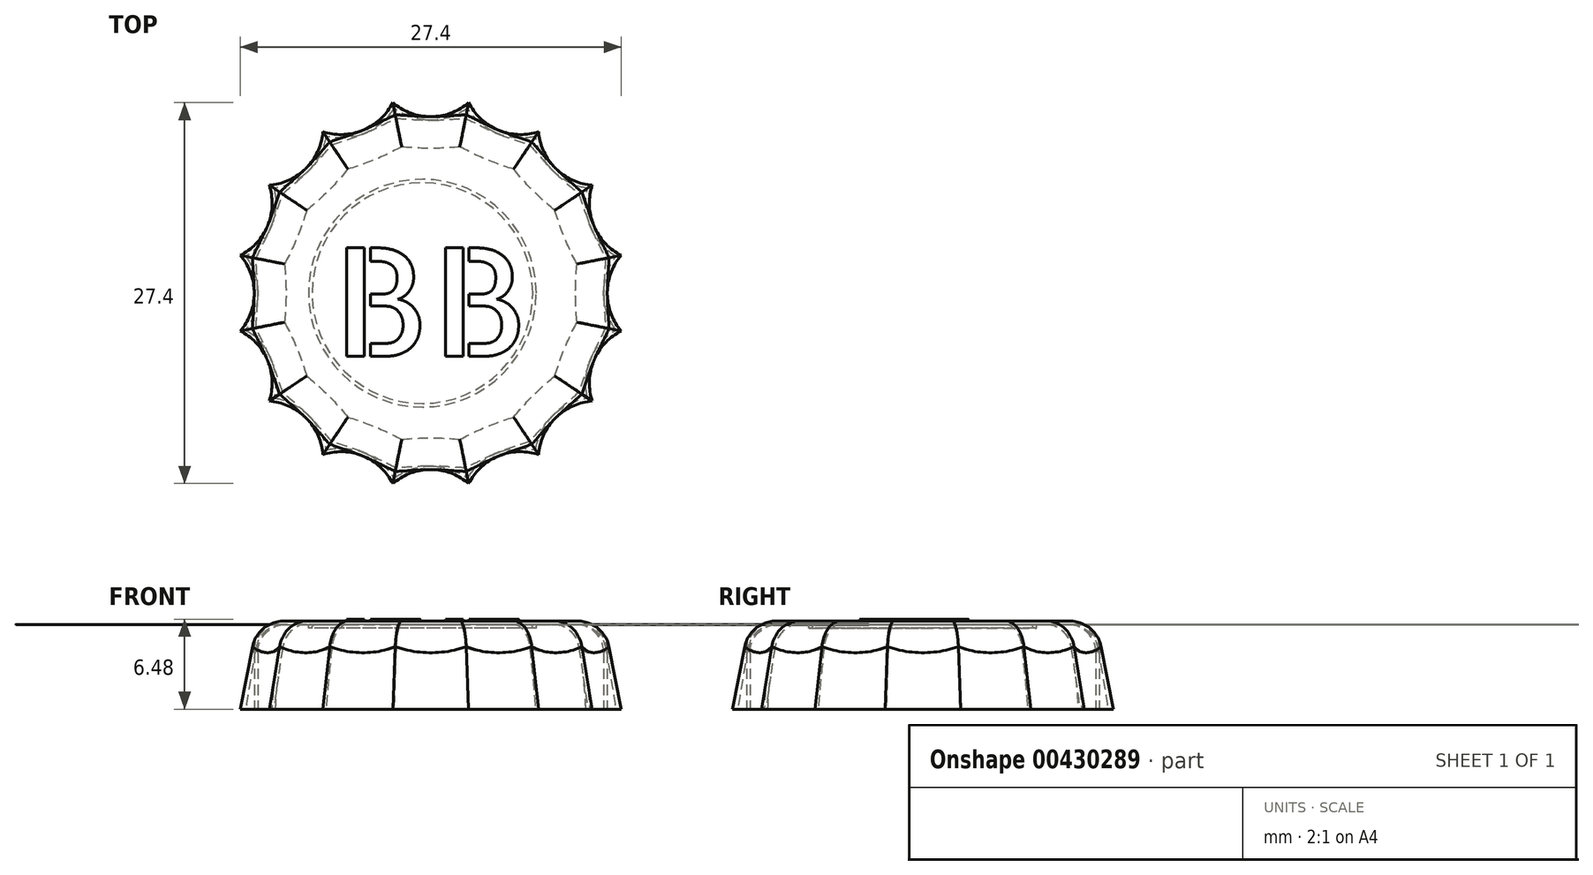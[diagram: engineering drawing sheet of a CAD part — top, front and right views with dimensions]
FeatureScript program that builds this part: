
annotation { "Feature Type Name" : "Feature", "Feature Type Description" : "" }
export const myFeature = defineFeature(function(context is Context, id is Id, definition is map)
    precondition{}
    {
        {
            var Q0;
            Q0=qCreatedBy(makeId("Top.planeOp"),FACE);
            var sketch = newSketch(context, id + "F0", { "sketchPlane" : qUnion([Q0])});
            skCircle(sketch, "E0", {"center": v(0, 0) * mm, "radius": 12.7 * mm, "construction": true});
            skCircle(sketch, "E1.0", {"center": v(0, 0) * mm, "radius": 13.97 * mm});
            skArc(sketch, "E2", {"start": v(-2.73, 13.7) * mm, "mid": v(0, 12.7) * mm, "end": v(2.73, 13.7) * mm});
            skArc(sketch, "E3.1.0", {"start": v(-7.76, 11.62) * mm, "mid": v(-4.86, 11.73) * mm, "end": v(-2.73, 13.7) * mm});
            skArc(sketch, "E3.2.0", {"start": v(-11.62, 7.76) * mm, "mid": v(-8.98, 8.98) * mm, "end": v(-7.76, 11.62) * mm});
            skArc(sketch, "E3.3.0", {"start": v(-13.7, 2.73) * mm, "mid": v(-11.73, 4.86) * mm, "end": v(-11.62, 7.76) * mm});
            skArc(sketch, "E3.4.0", {"start": v(-13.7, -2.73) * mm, "mid": v(-12.7, 0) * mm, "end": v(-13.7, 2.73) * mm});
            skArc(sketch, "E3.5.0", {"start": v(-11.62, -7.76) * mm, "mid": v(-11.73, -4.86) * mm, "end": v(-13.7, -2.73) * mm});
            skArc(sketch, "E3.6.0", {"start": v(-7.76, -11.62) * mm, "mid": v(-8.98, -8.98) * mm, "end": v(-11.62, -7.76) * mm});
            skArc(sketch, "E3.7.0", {"start": v(-2.73, -13.7) * mm, "mid": v(-4.86, -11.73) * mm, "end": v(-7.76, -11.62) * mm});
            skArc(sketch, "E3.8.0", {"start": v(2.73, -13.7) * mm, "mid": v(0, -12.7) * mm, "end": v(-2.73, -13.7) * mm});
            skArc(sketch, "E3.9.0", {"start": v(7.76, -11.62) * mm, "mid": v(4.86, -11.73) * mm, "end": v(2.73, -13.7) * mm});
            skArc(sketch, "E3.10.0", {"start": v(11.62, -7.76) * mm, "mid": v(8.98, -8.98) * mm, "end": v(7.76, -11.62) * mm});
            skArc(sketch, "E3.11.0", {"start": v(13.7, -2.73) * mm, "mid": v(11.73, -4.86) * mm, "end": v(11.62, -7.76) * mm});
            skArc(sketch, "E3.12.0", {"start": v(13.7, 2.73) * mm, "mid": v(12.7, 0) * mm, "end": v(13.7, -2.73) * mm});
            skArc(sketch, "E3.13.0", {"start": v(11.62, 7.76) * mm, "mid": v(11.73, 4.86) * mm, "end": v(13.7, 2.73) * mm});
            skArc(sketch, "E3.14.0", {"start": v(7.76, 11.62) * mm, "mid": v(8.98, 8.98) * mm, "end": v(11.62, 7.76) * mm});
            skArc(sketch, "E3.15.0", {"start": v(2.73, 13.7) * mm, "mid": v(4.86, 11.73) * mm, "end": v(7.76, 11.62) * mm});
            skSolve(sketch);
        }
        {
            var Q0;
            Q0=makeQuery(id+"F0.imprint","IMPRINT",FACE,{"disambiguationData":[TD([[makeQuery(id+"F0.imprint","IMPRINT",EDGE,{"derivedFrom":sQuery(id+"F0.wireOp",EDGE,"E2")}),-1.0]])]});
            var Q1;
            Q1 = qBodyType(qCreatedBy(id + "F2" ,EDGE), BodyType.WIRE);
            cPlane(context, id + "F1", {"entities" : qUnion([Q0, Q1]), "cplaneType" : CPlaneType.OFFSET, "offset" : 6.35 * mm, "width" : 152.4 * mm, "height" : 152.4 * mm});
        }
        {
            var Q0;
            Q0=qCreatedBy(id+"F1.planeOp",FACE);
            var sketch = newSketch(context, id + "F2", { "sketchPlane" : qUnion([Q0])});
            skCircle(sketch, "E4.0", {"center": v(0, 0) * mm, "radius": 12.7 * mm});
            skSolve(sketch);
        }
        {
            var Q0;
            Q0=makeQuery(id+"F0.imprint","IMPRINT",FACE,{"disambiguationData":[TD([[makeQuery(id+"F0.imprint","IMPRINT",EDGE,{"derivedFrom":sQuery(id+"F0.wireOp",EDGE,"E2")}),-1.0]])]});
            var Q1;
            Q1=makeQuery(id+"F2.imprint","IMPRINT",FACE,{"disambiguationData":[TD([[makeQuery(id+"F2.imprint","IMPRINT",EDGE,{"derivedFrom":sQuery(id+"F2.wireOp",EDGE,"E4.0")}),1.0]])]});
            loft(context, id + "F3", {"sheetProfilesArray" : [{ "sheetProfileEntities" : qUnion([Q0]) }, { "sheetProfileEntities" : qUnion([Q1]) }]});
        }
        {
            var Q0;
            Q0=makeQuery(id+"F3.opLoft","CAP_FACE",FACE,{"disambiguationData":[OSD([makeQuery(id+"F2.imprint","IMPRINT",FACE,{"disambiguationData":[TD([[makeQuery(id+"F2.imprint","IMPRINT",EDGE,{"derivedFrom":sQuery(id+"F2.wireOp",EDGE,"E4.0")}),1.0]])]})])],"isStart":true});
            fillet(context, id + "F4", {"entities" : qUnion([Q0]), "radius" : 2.3 * mm, "tangentPropagation" : true, "allowEdgeOverflow" : false});
        }
        {
            var Q0;
            Q0=makeQuery(id+"F3.opLoft","CAP_FACE",FACE,{"disambiguationData":[OSD([makeQuery(id+"F0.imprint","IMPRINT",FACE,{"disambiguationData":[TD([[makeQuery(id+"F0.imprint","IMPRINT",EDGE,{"derivedFrom":sQuery(id+"F0.wireOp",EDGE,"E2")}),-1.0]])]})])],"isStart":true});
            shell(context, id + "F5", {"entities" : qUnion([Q0]), "thickness" : 0.25 * mm});
        }
        {
            var Q0;
            Q0=makeQuery(id+"F3.opLoft","CAP_FACE",FACE,{"disambiguationData":[OSD([makeQuery(id+"F2.imprint","IMPRINT",FACE,{"disambiguationData":[TD([[makeQuery(id+"F2.imprint","IMPRINT",EDGE,{"derivedFrom":sQuery(id+"F2.wireOp",EDGE,"E4.0")}),1.0]])]})])],"isStart":true});
            cPlane(context, id + "F6", {"entities" : qUnion([Q0]), "cplaneType" : CPlaneType.OFFSET, "offset" : 0.25 * mm, "oppositeDirection" : true, "width" : 152.4 * mm, "height" : 152.4 * mm});
        }
        {
            var Q0;
            Q0=qCreatedBy(id+"F6.planeOp",FACE);
            var sketch = newSketch(context, id + "F7", { "sketchPlane" : qUnion([Q0])});
            skCircle(sketch, "E5", {"center": v(-0.6, 0) * mm, "radius": 7.94 * mm});
            skCircle(sketch, "E6.0", {"center": v(-0.6, 0) * mm, "radius": 8.2 * mm});
            skSolve(sketch);
        }
        {
            var Q0;
            Q0 = qSketchRegion(id + "F7", true);
            extrude(context, id + "F8", {"entities" : qUnion([Q0]), "operationType" : NewBodyOperationType.ADD, "oppositeDirection" : true, "depth" : 0.25 * mm});
        }
        {
            var Q0;
            Q0=makeQuery(id+"F8.opExtrude","CAP_EDGE",EDGE,{"disambiguationData":[OSD([sQuery(id+"F7.wireOp",EDGE,"E6.0")])],"isStart":true});
            var Q1;
            Q1=makeQuery(id+"F8.opExtrude","CAP_EDGE",EDGE,{"disambiguationData":[OSD([sQuery(id+"F7.wireOp",EDGE,"E5")])],"isStart":true});
            fillet(context, id + "F9", {"entities" : qUnion([Q0, Q1]), "radius" : 0.25 * mm, "tangentPropagation" : true, "allowEdgeOverflow" : false});
        }
        {
            var Q0;
            Q0=qCreatedBy(id+"F6.planeOp",FACE);
            var sketch = newSketch(context, id + "F10", { "sketchPlane" : qUnion([Q0])});
            skText(sketch, "E7", { "text": "BB", "fontName": "AllertaStencil-Regular.ttf"});
            const initialGuessF10  = {"E7": [-0.00706, -0.00454, 1, 0, 0.0078]};
            skSetInitialGuess(sketch, initialGuessF10);
            skSolve(sketch);
        }
        {
            var Q0;
            Q0 = qSketchRegion(id + "F10", true);
            extrude(context, id + "F11", {"entities" : qUnion([Q0]), "operationType" : NewBodyOperationType.ADD, "depth" : 0.38 * mm});
        }
    });
